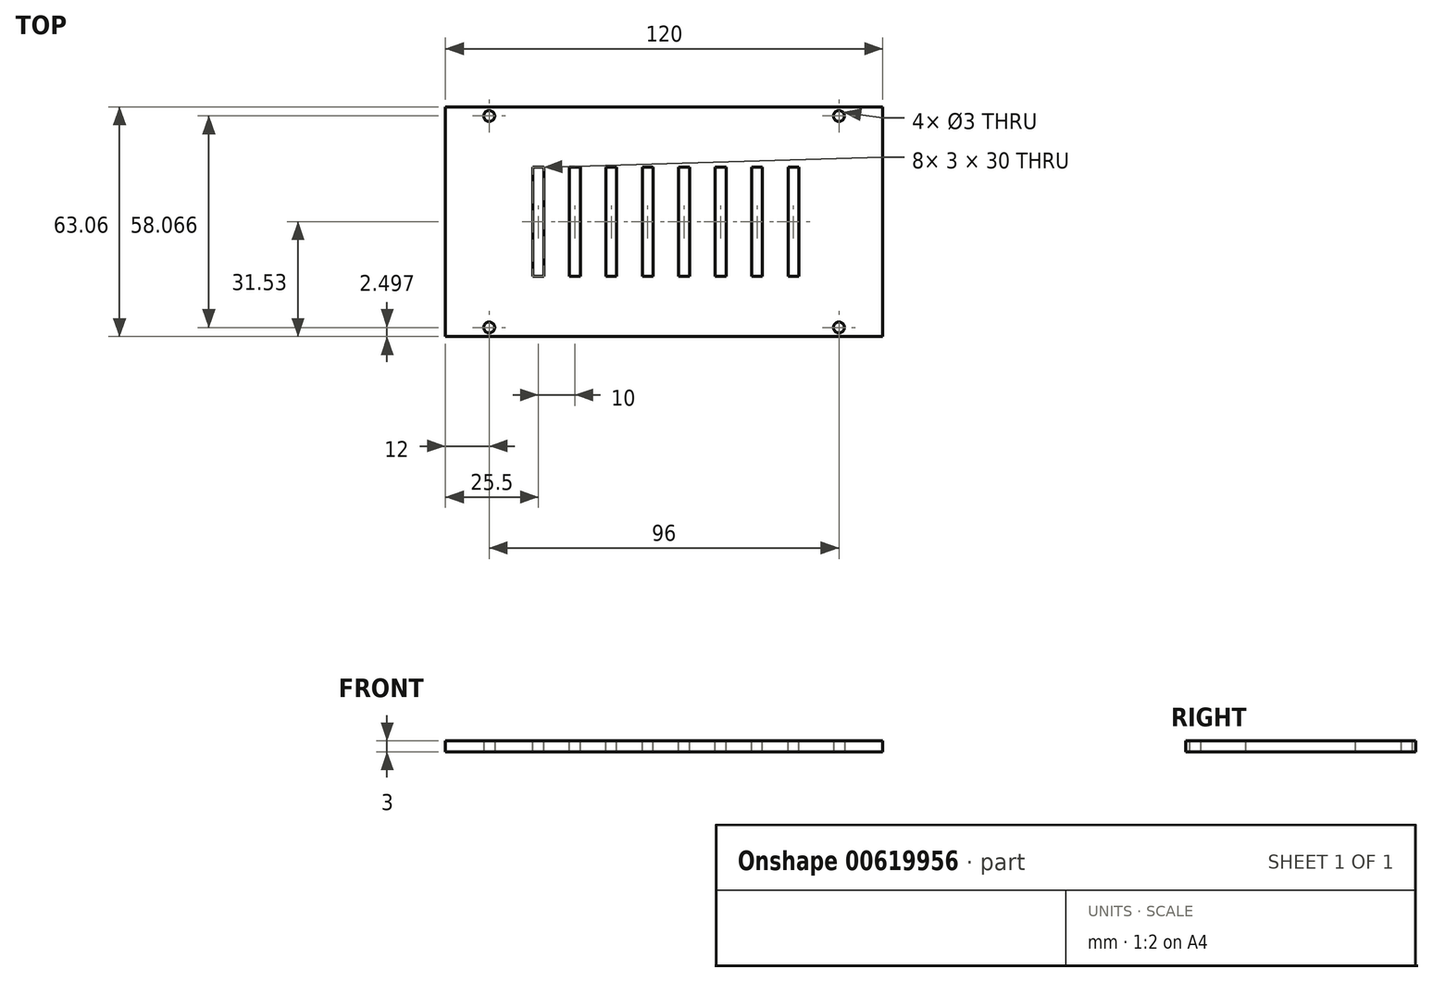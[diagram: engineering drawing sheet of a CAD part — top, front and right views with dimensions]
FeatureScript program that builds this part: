
annotation { "Feature Type Name" : "Feature", "Feature Type Description" : "" }
export const myFeature = defineFeature(function(context is Context, id is Id, definition is map)
    precondition{}
    {
        {
            var Q0;
            Q0=qCreatedBy(makeId("Top.planeOp"),FACE);
            var sketch = newSketch(context, id + "F0", { "sketchPlane" : qUnion([Q0])});
            skLineSegment(sketch, "E0.bottom", {"start": v(60, 31.53) * mm, "end": v(-60, 31.53) * mm});
            skLineSegment(sketch, "E0.top", {"start": v(60, -31.53) * mm, "end": v(-60, -31.53) * mm});
            skLineSegment(sketch, "E0.left", {"start": v(60, 31.53) * mm, "end": v(60, -31.53) * mm});
            skLineSegment(sketch, "E0.right", {"start": v(-60, 31.53) * mm, "end": v(-60, -31.53) * mm});
            skPoint(sketch, "E0.middle", {"position": v(0, 0) * mm});
            skSolve(sketch);
        }
        {
            var Q0;
            Q0 = qSketchRegion(id + "F0", true);
            extrude(context, id + "F1", {"entities" : qUnion([Q0]), "depth" : 3 * mm, "offsetDistance" : 25 * mm});
        }
        {
            var Q0;
            Q0=makeQuery(id+"F1.opExtrude","CAP_FACE",FACE,{"disambiguationData":[OSD([sQuery(id+"F0.wireOp",EDGE,"E0.bottom"),sQuery(id+"F0.wireOp",EDGE,"E0.top"),sQuery(id+"F0.wireOp",EDGE,"E0.left"),sQuery(id+"F0.wireOp",EDGE,"E0.right")])],"isStart":false});
            var sketch = newSketch(context, id + "F2", { "sketchPlane" : qUnion([Q0])});
            skPoint(sketch, "E1", {"position": v(48, 29.03) * mm});
            skLineSegment(sketch, "E2", {"start": v(0, 31.53) * mm, "end": v(0, -31.53) * mm, "construction": true});
            skLineSegment(sketch, "E3", {"start": v(60, 0) * mm, "end": v(-60, 0) * mm, "construction": true});
            skPoint(sketch, "E4.MirrorP", {"position": v(48, -29.03) * mm});
            skPoint(sketch, "E5.MirrorP", {"position": v(-48, -29.03) * mm});
            skPoint(sketch, "E6.MirrorP", {"position": v(-48, 29.03) * mm});
            skSolve(sketch);
        }
        {
            var Q0;
            Q0=sQuery(id+"F2.wireOp",VERTEX,"E6.MirrorP");
            var Q1;
            Q1=sQuery(id+"F2.wireOp",VERTEX,"E1");
            var Q2;
            Q2=sQuery(id+"F2.wireOp",VERTEX,"E4.MirrorP");
            var Q3;
            Q3=sQuery(id+"F2.wireOp",VERTEX,"E5.MirrorP");
            var Q4;
            Q4=makeQuery(id+"F1.opExtrude","SWEPT_BODY",BODY,{"disambiguationData":[OSD([sQuery(id+"F0.wireOp",EDGE,"E0.bottom"),sQuery(id+"F0.wireOp",EDGE,"E0.top"),sQuery(id+"F0.wireOp",EDGE,"E0.left"),sQuery(id+"F0.wireOp",EDGE,"E0.right")])]});
            hole(context, id + "F3", {"style" : HoleStyle.SIMPLE, "endStyle" : HoleEndStyle.THROUGH, "standardTappedOrClearance" : lookupTablePath({ "standard" : "ISO", "size" : "3", "type" : "Drilled" }), "standardBlindInLast" : lookupTablePath({ "standard" : "ISO", "size" : "3", "type" : "Drilled" }), "holeDiameter" : 3 * mm, "majorDiameter" : 3 * mm, "isTappedThrough" : true, "tappedDepth" : 21 * mm, "tapClearance" : 0, "locations" : qUnion([Q0, Q1, Q2, Q3]), "scope" : qUnion([Q4]), "startStyle" : HoleStartStyle.SKETCH});
        }
        {
            var Q0;
            Q0=makeQuery(id+"F1.opExtrude","CAP_FACE",FACE,{"disambiguationData":[OSD([sQuery(id+"F0.wireOp",EDGE,"E0.bottom"),sQuery(id+"F0.wireOp",EDGE,"E0.top"),sQuery(id+"F0.wireOp",EDGE,"E0.left"),sQuery(id+"F0.wireOp",EDGE,"E0.right")])],"isStart":false});
            var sketch = newSketch(context, id + "F4", { "sketchPlane" : qUnion([Q0])});
            skLineSegment(sketch, "E7.bottom", {"start": v(-33, 15) * mm, "end": v(-36, 15) * mm});
            skLineSegment(sketch, "E7.top", {"start": v(-33, -15) * mm, "end": v(-36, -15) * mm});
            skLineSegment(sketch, "E7.left", {"start": v(-33, 15) * mm, "end": v(-33, -15) * mm});
            skLineSegment(sketch, "E7.right", {"start": v(-36, 15) * mm, "end": v(-36, -15) * mm});
            skPoint(sketch, "E7.middle", {"position": v(-34.5, 0) * mm});
            skLineSegment(sketch, "E8.1.0.0", {"start": v(-23, 15) * mm, "end": v(-23, -15) * mm});
            skLineSegment(sketch, "E8.1.0.1", {"start": v(-26, 15) * mm, "end": v(-26, -15) * mm});
            skPoint(sketch, "E8.1.0.2", {"position": v(-24.5, 0) * mm});
            skLineSegment(sketch, "E8.1.0.3", {"start": v(-23, -15) * mm, "end": v(-26, -15) * mm});
            skLineSegment(sketch, "E8.1.0.4", {"start": v(-23, 15) * mm, "end": v(-26, 15) * mm});
            skLineSegment(sketch, "E8.2.0.0", {"start": v(-13, 15) * mm, "end": v(-13, -15) * mm});
            skLineSegment(sketch, "E8.2.0.1", {"start": v(-16, 15) * mm, "end": v(-16, -15) * mm});
            skPoint(sketch, "E8.2.0.2", {"position": v(-14.5, 0) * mm});
            skLineSegment(sketch, "E8.2.0.3", {"start": v(-13, -15) * mm, "end": v(-16, -15) * mm});
            skLineSegment(sketch, "E8.2.0.4", {"start": v(-13, 15) * mm, "end": v(-16, 15) * mm});
            skLineSegment(sketch, "E8.3.0.0", {"start": v(-3, 15) * mm, "end": v(-3, -15) * mm});
            skLineSegment(sketch, "E8.3.0.1", {"start": v(-6, 15) * mm, "end": v(-6, -15) * mm});
            skPoint(sketch, "E8.3.0.2", {"position": v(-4.5, 0) * mm});
            skLineSegment(sketch, "E8.3.0.3", {"start": v(-3, -15) * mm, "end": v(-6, -15) * mm});
            skLineSegment(sketch, "E8.3.0.4", {"start": v(-3, 15) * mm, "end": v(-6, 15) * mm});
            skLineSegment(sketch, "E8.4.0.0", {"start": v(7, 15) * mm, "end": v(7, -15) * mm});
            skLineSegment(sketch, "E8.4.0.1", {"start": v(4, 15) * mm, "end": v(4, -15) * mm});
            skPoint(sketch, "E8.4.0.2", {"position": v(5.5, 0) * mm});
            skLineSegment(sketch, "E8.4.0.3", {"start": v(7, -15) * mm, "end": v(4, -15) * mm});
            skLineSegment(sketch, "E8.4.0.4", {"start": v(7, 15) * mm, "end": v(4, 15) * mm});
            skLineSegment(sketch, "E8.5.0.0", {"start": v(17, 15) * mm, "end": v(17, -15) * mm});
            skLineSegment(sketch, "E8.5.0.1", {"start": v(14, 15) * mm, "end": v(14, -15) * mm});
            skPoint(sketch, "E8.5.0.2", {"position": v(15.5, 0) * mm});
            skLineSegment(sketch, "E8.5.0.3", {"start": v(17, -15) * mm, "end": v(14, -15) * mm});
            skLineSegment(sketch, "E8.5.0.4", {"start": v(17, 15) * mm, "end": v(14, 15) * mm});
            skLineSegment(sketch, "E8.6.0.0", {"start": v(27, 15) * mm, "end": v(27, -15) * mm});
            skLineSegment(sketch, "E8.6.0.1", {"start": v(24, 15) * mm, "end": v(24, -15) * mm});
            skPoint(sketch, "E8.6.0.2", {"position": v(25.5, 0) * mm});
            skLineSegment(sketch, "E8.6.0.3", {"start": v(27, -15) * mm, "end": v(24, -15) * mm});
            skLineSegment(sketch, "E8.6.0.4", {"start": v(27, 15) * mm, "end": v(24, 15) * mm});
            skLineSegment(sketch, "E8.7.0.0", {"start": v(37, 15) * mm, "end": v(37, -15) * mm});
            skLineSegment(sketch, "E8.7.0.1", {"start": v(34, 15) * mm, "end": v(34, -15) * mm});
            skPoint(sketch, "E8.7.0.2", {"position": v(35.5, 0) * mm});
            skLineSegment(sketch, "E8.7.0.3", {"start": v(37, -15) * mm, "end": v(34, -15) * mm});
            skLineSegment(sketch, "E8.7.0.4", {"start": v(37, 15) * mm, "end": v(34, 15) * mm});
            skLineSegment(sketch, "E8.direction1", {"start": v(-36, -15) * mm, "end": v(-26, -15) * mm, "construction": true});
            skSolve(sketch);
        }
        {
            var Q0;
            Q0=makeQuery(id+"F4.imprint","IMPRINT",FACE,{"disambiguationData":[TD([[makeQuery(id+"F4.imprint","IMPRINT",EDGE,{"derivedFrom":sQuery(id+"F4.wireOp",EDGE,"E7.bottom")}),1.0]])]});
            var Q1;
            Q1=makeQuery(id+"F4.imprint","IMPRINT",FACE,{"disambiguationData":[TD([[makeQuery(id+"F4.imprint","IMPRINT",EDGE,{"derivedFrom":sQuery(id+"F4.wireOp",EDGE,"E8.1.0.0")}),-1.0]])]});
            var Q2;
            Q2=makeQuery(id+"F4.imprint","IMPRINT",FACE,{"disambiguationData":[TD([[makeQuery(id+"F4.imprint","IMPRINT",EDGE,{"derivedFrom":sQuery(id+"F4.wireOp",EDGE,"E8.2.0.0")}),-1.0]])]});
            var Q3;
            Q3=makeQuery(id+"F4.imprint","IMPRINT",FACE,{"disambiguationData":[TD([[makeQuery(id+"F4.imprint","IMPRINT",EDGE,{"derivedFrom":sQuery(id+"F4.wireOp",EDGE,"E8.4.0.0")}),-1.0]])]});
            var Q4;
            Q4=makeQuery(id+"F4.imprint","IMPRINT",FACE,{"disambiguationData":[TD([[makeQuery(id+"F4.imprint","IMPRINT",EDGE,{"derivedFrom":sQuery(id+"F4.wireOp",EDGE,"E8.3.0.0")}),-1.0]])]});
            var Q5;
            Q5=makeQuery(id+"F4.imprint","IMPRINT",FACE,{"disambiguationData":[TD([[makeQuery(id+"F4.imprint","IMPRINT",EDGE,{"derivedFrom":sQuery(id+"F4.wireOp",EDGE,"E8.5.0.0")}),-1.0]])]});
            var Q6;
            Q6=makeQuery(id+"F4.imprint","IMPRINT",FACE,{"disambiguationData":[TD([[makeQuery(id+"F4.imprint","IMPRINT",EDGE,{"derivedFrom":sQuery(id+"F4.wireOp",EDGE,"E8.6.0.0")}),-1.0]])]});
            var Q7;
            Q7=makeQuery(id+"F4.imprint","IMPRINT",FACE,{"disambiguationData":[TD([[makeQuery(id+"F4.imprint","IMPRINT",EDGE,{"derivedFrom":sQuery(id+"F4.wireOp",EDGE,"E8.7.0.0")}),-1.0]])]});
            extrude(context, id + "F5", {"entities" : qUnion([Q0, Q1, Q2, Q3, Q4, Q5, Q6, Q7]), "operationType" : NewBodyOperationType.REMOVE, "endBound" : BoundingType.THROUGH_ALL, "oppositeDirection" : true, "depth" : 25 * mm, "offsetDistance" : 25 * mm});
        }
    });
